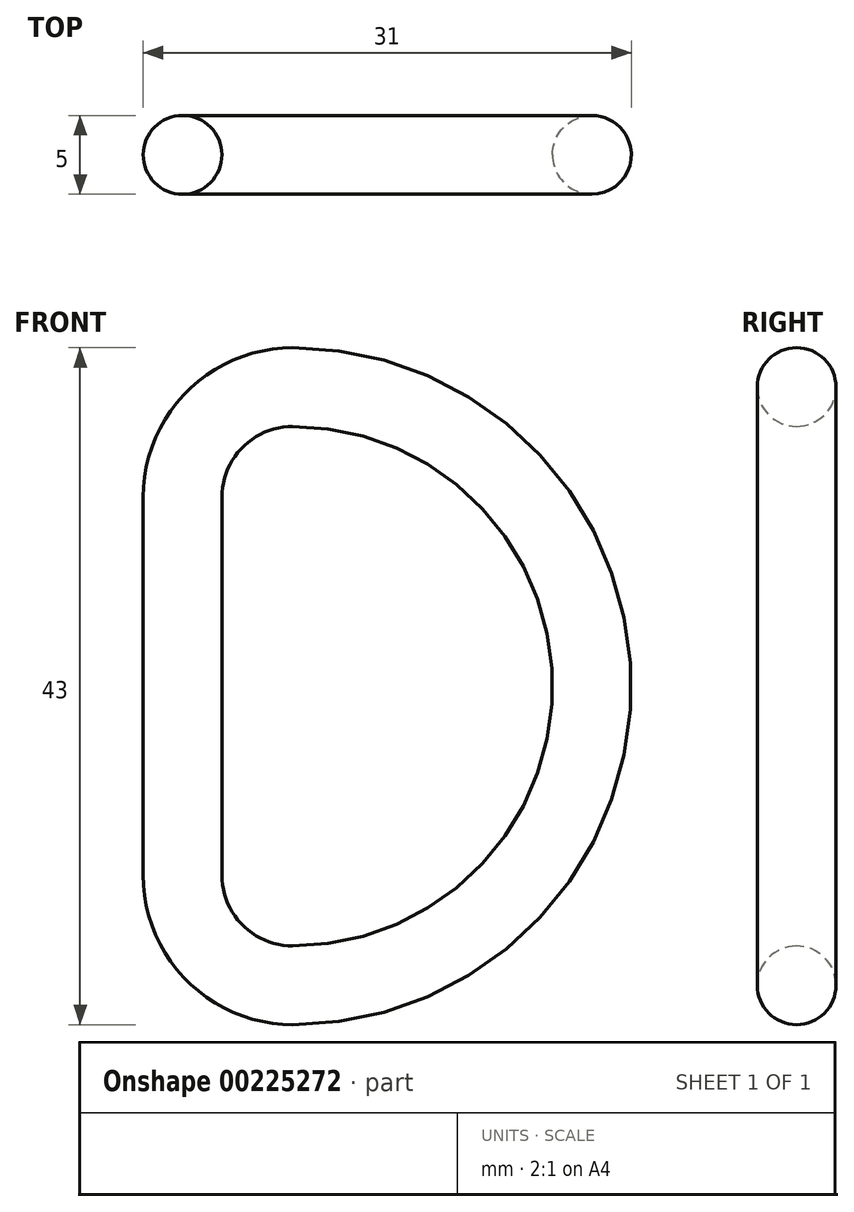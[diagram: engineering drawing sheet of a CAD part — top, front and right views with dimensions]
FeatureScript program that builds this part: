
annotation { "Feature Type Name" : "Feature", "Feature Type Description" : "" }
export const myFeature = defineFeature(function(context is Context, id is Id, definition is map)
    precondition{}
    {
        {
            var Q0;
            Q0=qCreatedBy(makeId("Front.planeOp"),FACE);
            var sketch = newSketch(context, id + "F0", { "sketchPlane" : qUnion([Q0])});
            skLineSegment(sketch, "E0", {"start": v(0, 0) * mm, "end": v(0, 12) * mm});
            skLineSegment(sketch, "E1.MirrorCS", {"start": v(0, 0) * mm, "end": v(0, -12) * mm});
            skArc(sketch, "E2", {"start": v(7, -19) * mm, "mid": v(26, 0) * mm, "end": v(7, 19) * mm});
            skPoint(sketch, "E3.MirrorCS.end.orphan", {"position": v(0, -12) * mm});
            skArc(sketch, "E4", {"start": v(7, 19) * mm, "mid": v(2.05, 16.95) * mm, "end": v(0, 12) * mm});
            skArc(sketch, "E5.MirrorCS", {"start": v(7, -19) * mm, "mid": v(2.05, -16.95) * mm, "end": v(0, -12) * mm});
            skSolve(sketch);
        }
        {
            var Q0;
            Q0=qCreatedBy(makeId("Top.planeOp"),FACE);
            var sketch = newSketch(context, id + "F1", { "sketchPlane" : qUnion([Q0])});
            skCircle(sketch, "E6", {"center": v(0, 0) * mm, "radius": 2.5 * mm});
            skSolve(sketch);
        }
        {
            var Q0;
            Q0=makeQuery(id+"F1.imprint","IMPRINT",FACE,{"disambiguationData":[TD([[makeQuery(id+"F1.imprint","IMPRINT",EDGE,{"derivedFrom":sQuery(id+"F1.wireOp",EDGE,"E6")}),1.0]])]});
            var Q1;
            Q1=sQuery(id+"F0.wireOp",EDGE,"E0");
            var Q2;
            Q2=sQuery(id+"F0.wireOp",EDGE,"E4");
            var Q3;
            Q3=sQuery(id+"F0.wireOp",EDGE,"E2");
            var Q4;
            Q4=sQuery(id+"F0.wireOp",EDGE,"E1.MirrorCS");
            var Q5;
            Q5=sQuery(id+"F0.wireOp",EDGE,"E5.MirrorCS");
            sweep(context, id + "F2", {"profiles" : qUnion([Q0]), "path" : qUnion([Q1, Q2, Q3, Q4, Q5])});
        }
    });
